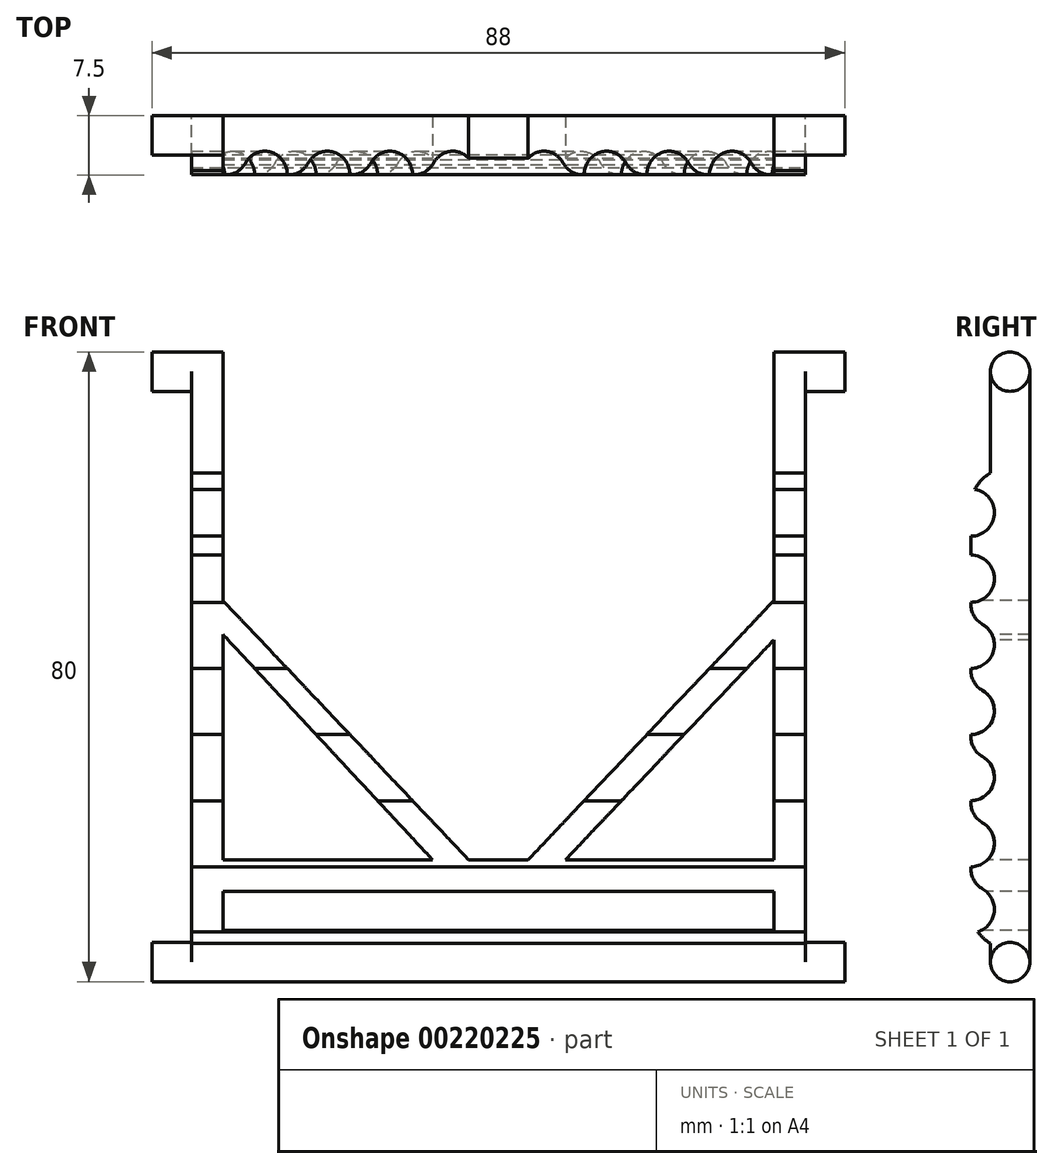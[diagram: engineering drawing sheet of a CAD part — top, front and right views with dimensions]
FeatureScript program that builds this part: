
annotation { "Feature Type Name" : "Feature", "Feature Type Description" : "" }
export const myFeature = defineFeature(function(context is Context, id is Id, definition is map)
    precondition{}
    {
        {
            var Q0;
            Q0=qCreatedBy(makeId("Right.planeOp"),FACE);
            var sketch = newSketch(context, id + "F0", { "sketchPlane" : qUnion([Q0])});
            skLineSegment(sketch, "E0.bottom", {"start": v(-4.18, 3.38) * mm, "end": v(0.82, 3.38) * mm});
            skLineSegment(sketch, "E0.top", {"start": v(-4.18, -71.62) * mm, "end": v(0.82, -71.62) * mm});
            skLineSegment(sketch, "E0.left", {"start": v(-4.18, 3.38) * mm, "end": v(-4.18, -71.62) * mm});
            skLineSegment(sketch, "E0.right", {"start": v(0.82, 3.38) * mm, "end": v(0.82, -71.62) * mm});
            skCircle(sketch, "E1", {"center": v(-1.68, 3.38) * mm, "radius": 2.5 * mm});
            skCircle(sketch, "E2", {"center": v(-1.68, -71.62) * mm, "radius": 2.5 * mm});
            skLineSegment(sketch, "E3.bottom", {"start": v(-4.18, -69.26) * mm, "end": v(-6.68, -69.26) * mm});
            skLineSegment(sketch, "E3.top", {"start": v(-4.18, -9.5) * mm, "end": v(-6.68, -9.5) * mm});
            skLineSegment(sketch, "E3.left", {"start": v(-4.18, -69.26) * mm, "end": v(-4.18, -9.5) * mm});
            skLineSegment(sketch, "E3.right", {"start": v(-6.68, -69.26) * mm, "end": v(-6.68, -9.5) * mm});
            skSolve(sketch);
        }
        {
            var Q0;
            {var subQ0=sQuery(id+"F0.wireOp",EDGE,"E0.left");Q0=makeQuery(id+"F0.imprint","IMPRINT",FACE,{"disambiguationData":[TD([[makeQuery(id+"F0.imprint","IMPRINT",EDGE,{"derivedFrom":subQ0}),1.0]])]});}
            extrude(context, id + "F1", {"entities" : qUnion([Q0]), "endBound" : BoundingType.SYMMETRIC, "depth" : 78 * mm});
        }
        {
            var Q0;
            Q0=makeQuery(id+"F0.imprint","IMPRINT",FACE,{"disambiguationData":[TD([[makeQuery(id+"F0.imprint","IMPRINT",EDGE,{"derivedFrom":sQuery(id+"F0.wireOp",EDGE,"E3.bottom")}),-1.0]])]});
            extrude(context, id + "F2", {"entities" : qUnion([Q0]), "operationType" : NewBodyOperationType.ADD, "endBound" : BoundingType.SYMMETRIC, "depth" : 78 * mm});
        }
        {
            var Q0;
            {var subQ0=sQuery(id+"F0.wireOp",EDGE,"E0.bottom");Q0=makeQuery(id+"F0.imprint","IMPRINT",FACE,{"disambiguationData":[TD([[makeQuery(id+"F0.imprint","IMPRINT",EDGE,{"derivedFrom":subQ0}),1.0]])]});}
            var Q1;
            {var subQ0=sQuery(id+"F0.wireOp",EDGE,"E0.bottom");Q1=makeQuery(id+"F0.imprint","IMPRINT",FACE,{"disambiguationData":[TD([[makeQuery(id+"F0.imprint","IMPRINT",EDGE,{"derivedFrom":subQ0}),-1.0]])]});}
            var Q2;
            {var subQ0=sQuery(id+"F0.wireOp",EDGE,"E0.top");Q2=makeQuery(id+"F0.imprint","IMPRINT",FACE,{"disambiguationData":[TD([[makeQuery(id+"F0.imprint","IMPRINT",EDGE,{"derivedFrom":subQ0}),-1.0]])]});}
            var Q3;
            {var subQ0=sQuery(id+"F0.wireOp",EDGE,"E0.top");Q3=makeQuery(id+"F0.imprint","IMPRINT",FACE,{"disambiguationData":[TD([[makeQuery(id+"F0.imprint","IMPRINT",EDGE,{"derivedFrom":subQ0}),1.0]])]});}
            extrude(context, id + "F3", {"entities" : qUnion([Q0, Q1, Q2, Q3]), "operationType" : NewBodyOperationType.ADD, "endBound" : BoundingType.SYMMETRIC, "depth" : 88 * mm});
        }
        {
            var Q0;
            Q0=makeQuery(id+"F1.opExtrude","SWEPT_FACE",FACE,{"disambiguationData":[OSD([sQuery(id+"F0.wireOp",EDGE,"E0.right")])]});
            var sketch = newSketch(context, id + "F4", { "sketchPlane" : qUnion([Q0])});
            skLineSegment(sketch, "E4.0", {"start": v(39, 3.38) * mm, "end": v(39, -71.62) * mm});
            skLineSegment(sketch, "E4.1", {"start": v(39, 3.38) * mm, "end": v(39, -9.5) * mm});
            skLineSegment(sketch, "E5.bottom", {"start": v(-35, -62.62) * mm, "end": v(35, -62.62) * mm});
            skLineSegment(sketch, "E5.top", {"start": v(-35, -67.62) * mm, "end": v(35, -67.62) * mm});
            skLineSegment(sketch, "E5.left", {"start": v(-35, -62.62) * mm, "end": v(-35, -67.62) * mm});
            skLineSegment(sketch, "E5.right", {"start": v(35, -62.62) * mm, "end": v(35, -67.62) * mm});
            skLineSegment(sketch, "E6.bottom", {"start": v(35, 7.25) * mm, "end": v(-35, 7.25) * mm});
            skLineSegment(sketch, "E6.top", {"start": v(35, -58.62) * mm, "end": v(-35, -58.62) * mm});
            skLineSegment(sketch, "E6.left", {"start": v(35, 7.25) * mm, "end": v(35, -58.62) * mm});
            skLineSegment(sketch, "E6.right", {"start": v(-35, 7.25) * mm, "end": v(-35, -58.62) * mm});
            skLineSegment(sketch, "E7", {"start": v(-35, -25.69) * mm, "end": v(0, -62.62) * mm});
            skLineSegment(sketch, "E8", {"start": v(0, -62.62) * mm, "end": v(35, -25.69) * mm});
            skLineSegment(sketch, "E9", {"start": v(35, -25.69) * mm, "end": v(39, -25.69) * mm});
            skLineSegment(sketch, "E10", {"start": v(39, -25.69) * mm, "end": v(0, -67.62) * mm});
            skLineSegment(sketch, "E11", {"start": v(0, -67.62) * mm, "end": v(-39.74, -25.69) * mm});
            skLineSegment(sketch, "E12", {"start": v(-39.74, -25.69) * mm, "end": v(-35, -25.69) * mm});
            skSolve(sketch);
        }
        {
            var Q0;
            {var subQ0=sQuery(id+"F0.wireOp",EDGE,"E3.top");var subQ1=sQuery(id+"F0.wireOp",EDGE,"E3.right");Q0=makeQuery(id+"F17sXBwQNLpgOEj_1.boolean.opBoolean","SPLIT",EDGE,{"disambiguationData":[TD([makeQuery(id+"F17sXBwQNLpgOEj_1.opExtrude","SWEPT_FACE",FACE,{"disambiguationData":[OSD([sQuery(id+"F4.wireOp",EDGE,"E6.left")])]})])],"derivedFrom":makeQuery(id+"F2.opExtrude","SWEPT_EDGE",EDGE,{"disambiguationData":[OSD([subQ0,subQ1])]})});}
            var Q1;
            {var subQ0=sQuery(id+"F0.wireOp",EDGE,"E3.top");var subQ1=sQuery(id+"F0.wireOp",EDGE,"E3.right");Q1=makeQuery(id+"F17sXBwQNLpgOEj_1.boolean.opBoolean","SPLIT",EDGE,{"disambiguationData":[TD([makeQuery(id+"F17sXBwQNLpgOEj_1.opExtrude","SWEPT_FACE",FACE,{"disambiguationData":[OSD([sQuery(id+"F4.wireOp",EDGE,"E6.right")])]})])],"derivedFrom":makeQuery(id+"F2.opExtrude","SWEPT_EDGE",EDGE,{"disambiguationData":[OSD([subQ0,subQ1])]})});}
            var Q2;
            Q2=makeQuery(id+"F2.opExtrude","SWEPT_EDGE",EDGE,{"disambiguationData":[OSD([sQuery(id+"F0.wireOp",EDGE,"E3.bottom"),sQuery(id+"F0.wireOp",EDGE,"E3.right")])]});
            fillet(context, id + "F5", {"entities" : qUnion([Q0, Q1, Q2]), "radius" : 5 * mm, "tangentPropagation" : true, "allowEdgeOverflow" : false});
        }
        {
            var Q0;
            {var subQ0=sQuery(id+"F0.wireOp",EDGE,"E3.left");Q0=makeQuery(id+"F2.boolean.opBoolean","MERGE",FACE,{"derivedFrom":[makeQuery(id+"F1.opExtrude","CAP_FACE",FACE,{"disambiguationData":[OSD([sQuery(id+"F0.wireOp",EDGE,"E0.left"),sQuery(id+"F0.wireOp",EDGE,"E0.right"),sQuery(id+"F0.wireOp",EDGE,"E1"),sQuery(id+"F0.wireOp",EDGE,"E2"),subQ0])],"isStart":false}),makeQuery(id+"F2.opExtrude","CAP_FACE",FACE,{"disambiguationData":[OSD([sQuery(id+"F0.wireOp",EDGE,"E3.bottom"),sQuery(id+"F0.wireOp",EDGE,"E3.top"),subQ0,sQuery(id+"F0.wireOp",EDGE,"E3.right")])],"isStart":false})]});}
            var sketch = newSketch(context, id + "F6", { "sketchPlane" : qUnion([Q0])});
            skCircle(sketch, "E13", {"center": v(-6.68, -64.93) * mm, "radius": 3 * mm});
            skCircle(sketch, "E14.0.1.0", {"center": v(-6.68, -56.53) * mm, "radius": 3 * mm});
            skCircle(sketch, "E14.0.2.0", {"center": v(-6.68, -48.13) * mm, "radius": 3 * mm});
            skCircle(sketch, "E14.0.3.0", {"center": v(-6.68, -39.73) * mm, "radius": 3 * mm});
            skCircle(sketch, "E14.0.4.0", {"center": v(-6.68, -31.33) * mm, "radius": 3 * mm});
            skCircle(sketch, "E14.0.5.0", {"center": v(-6.68, -22.93) * mm, "radius": 3 * mm});
            skCircle(sketch, "E14.0.6.0", {"center": v(-6.68, -14.53) * mm, "radius": 3 * mm});
            skLineSegment(sketch, "E14.direction1", {"start": v(-6.68, -64.93) * mm, "end": v(18.32, -64.93) * mm, "construction": true});
            skLineSegment(sketch, "E14.direction2", {"start": v(-6.68, -64.93) * mm, "end": v(-6.68, -56.53) * mm, "construction": true});
            skSolve(sketch);
        }
        {
            var Q0;
            {var subQ0=sQuery(id+"F6.wireOp",EDGE,"E13");var subQ1=sQuery(id+"F0.wireOp",EDGE,"E3.right");var subQ6=makeQuery(id+"F2.opExtrude","CAP_EDGE",EDGE,{"disambiguationData":[OSD([subQ1])],"isStart":false});var subQ7=makeQuery(id+"F6.imprint","INTERSECT",VERTEX,{"derivedFrom":[subQ6,subQ0]});Q0=makeQuery(id+"F6.imprint","IMPRINT",FACE,{"disambiguationData":[TD([[makeQuery(id+"F6.imprint","IMPRINT",EDGE,{"disambiguationData":[TD([[subQ7,1.0]])],"derivedFrom":subQ0}),1.0]])]});}
            var Q1;
            {var subQ0=sQuery(id+"F6.wireOp",EDGE,"E14.0.1.0");var subQ1=makeQuery(id+"F2.opExtrude","CAP_EDGE",EDGE,{"disambiguationData":[OSD([sQuery(id+"F0.wireOp",EDGE,"E3.right")])],"isStart":false});var subQ2=makeQuery(id+"F6.imprint","INTERSECT",VERTEX,{"disambiguationData":[OD(0.0)],"derivedFrom":[subQ1,subQ0]});Q1=makeQuery(id+"F6.imprint","IMPRINT",FACE,{"disambiguationData":[TD([[makeQuery(id+"F6.imprint","IMPRINT",EDGE,{"disambiguationData":[TD([[subQ2,-1.0]])],"derivedFrom":subQ0}),1.0]])]});}
            var Q2;
            {var subQ0=sQuery(id+"F6.wireOp",EDGE,"E14.0.2.0");var subQ1=makeQuery(id+"F2.opExtrude","CAP_EDGE",EDGE,{"disambiguationData":[OSD([sQuery(id+"F0.wireOp",EDGE,"E3.right")])],"isStart":false});var subQ2=makeQuery(id+"F6.imprint","INTERSECT",VERTEX,{"disambiguationData":[OD(0.0)],"derivedFrom":[subQ1,subQ0]});Q2=makeQuery(id+"F6.imprint","IMPRINT",FACE,{"disambiguationData":[TD([[makeQuery(id+"F6.imprint","IMPRINT",EDGE,{"disambiguationData":[TD([[subQ2,-1.0]])],"derivedFrom":subQ0}),1.0]])]});}
            var Q3;
            {var subQ0=sQuery(id+"F6.wireOp",EDGE,"E14.0.3.0");var subQ1=makeQuery(id+"F2.opExtrude","CAP_EDGE",EDGE,{"disambiguationData":[OSD([sQuery(id+"F0.wireOp",EDGE,"E3.right")])],"isStart":false});var subQ2=makeQuery(id+"F6.imprint","INTERSECT",VERTEX,{"disambiguationData":[OD(0.0)],"derivedFrom":[subQ1,subQ0]});Q3=makeQuery(id+"F6.imprint","IMPRINT",FACE,{"disambiguationData":[TD([[makeQuery(id+"F6.imprint","IMPRINT",EDGE,{"disambiguationData":[TD([[subQ2,-1.0]])],"derivedFrom":subQ0}),1.0]])]});}
            var Q4;
            {var subQ0=sQuery(id+"F6.wireOp",EDGE,"E14.0.4.0");var subQ1=makeQuery(id+"F2.opExtrude","CAP_EDGE",EDGE,{"disambiguationData":[OSD([sQuery(id+"F0.wireOp",EDGE,"E3.right")])],"isStart":false});var subQ2=makeQuery(id+"F6.imprint","INTERSECT",VERTEX,{"disambiguationData":[OD(0.0)],"derivedFrom":[subQ1,subQ0]});Q4=makeQuery(id+"F6.imprint","IMPRINT",FACE,{"disambiguationData":[TD([[makeQuery(id+"F6.imprint","IMPRINT",EDGE,{"disambiguationData":[TD([[subQ2,1.0]])],"derivedFrom":subQ0}),1.0]])]});}
            var Q5;
            {var subQ0=sQuery(id+"F6.wireOp",EDGE,"E14.0.5.0");var subQ1=makeQuery(id+"F2.opExtrude","CAP_EDGE",EDGE,{"disambiguationData":[OSD([sQuery(id+"F0.wireOp",EDGE,"E3.right")])],"isStart":false});var subQ2=makeQuery(id+"F6.imprint","INTERSECT",VERTEX,{"disambiguationData":[OD(0.0)],"derivedFrom":[subQ1,subQ0]});Q5=makeQuery(id+"F6.imprint","IMPRINT",FACE,{"disambiguationData":[TD([[makeQuery(id+"F6.imprint","IMPRINT",EDGE,{"disambiguationData":[TD([[subQ2,1.0]])],"derivedFrom":subQ0}),1.0]])]});}
            var Q6;
            {var subQ0=sQuery(id+"F6.wireOp",EDGE,"E14.0.6.0");var subQ1=sQuery(id+"F0.wireOp",EDGE,"E3.right");var subQ8=makeQuery(id+"F2.opExtrude","CAP_EDGE",EDGE,{"disambiguationData":[OSD([subQ1])],"isStart":false});var subQ9=makeQuery(id+"F6.imprint","INTERSECT",VERTEX,{"derivedFrom":[subQ8,subQ0]});Q6=makeQuery(id+"F6.imprint","IMPRINT",FACE,{"disambiguationData":[TD([[makeQuery(id+"F6.imprint","IMPRINT",EDGE,{"disambiguationData":[TD([[subQ9,-1.0]])],"derivedFrom":subQ0}),1.0]])]});}
            extrude(context, id + "F7", {"entities" : qUnion([Q0, Q1, Q2, Q3, Q4, Q5, Q6]), "operationType" : NewBodyOperationType.REMOVE, "endBound" : BoundingType.THROUGH_ALL, "oppositeDirection" : true, "depth" : 25 * mm});
        }
        {
            var Q0;
            {var subQ3=sQuery(id+"F4.wireOp",EDGE,"E6.top");var subQ5=sQuery(id+"F4.wireOp",EDGE,"E8");var subQ6=makeQuery(id+"F4.imprint","INTERSECT",VERTEX,{"derivedFrom":[subQ3,subQ5]});Q0=makeQuery(id+"F4.imprint","IMPRINT",FACE,{"disambiguationData":[TD([[makeQuery(id+"F4.imprint","IMPRINT",EDGE,{"disambiguationData":[TD([[subQ6,-1.0]])],"derivedFrom":subQ3}),-1.0]])]});}
            var Q1;
            {var subQ0=sQuery(id+"F4.wireOp",EDGE,"E6.bottom");Q1=makeQuery(id+"F4.imprint","IMPRINT",FACE,{"disambiguationData":[TD([[makeQuery(id+"F4.imprint","IMPRINT",EDGE,{"derivedFrom":subQ0}),1.0]])]});}
            var Q2;
            {var subQ0=sQuery(id+"F4.wireOp",EDGE,"E6.right");var subQ1=sQuery(id+"F4.wireOp",EDGE,"E6.top");var subQ2=makeQuery(id+"F4.imprint","INTERSECT",VERTEX,{"derivedFrom":[subQ1,subQ0]});Q2=makeQuery(id+"F4.imprint","IMPRINT",FACE,{"disambiguationData":[TD([[makeQuery(id+"F4.imprint","IMPRINT",EDGE,{"disambiguationData":[TD([[subQ2,1.0]])],"derivedFrom":subQ1}),-1.0]])]});}
            var Q3;
            {var subQ0=sQuery(id+"F4.wireOp",EDGE,"E5.left");Q3=makeQuery(id+"F4.imprint","IMPRINT",FACE,{"disambiguationData":[TD([[makeQuery(id+"F4.imprint","IMPRINT",EDGE,{"derivedFrom":subQ0}),1.0]])]});}
            var Q4;
            {var subQ0=sQuery(id+"F4.wireOp",EDGE,"E5.right");Q4=makeQuery(id+"F4.imprint","IMPRINT",FACE,{"disambiguationData":[TD([[makeQuery(id+"F4.imprint","IMPRINT",EDGE,{"derivedFrom":subQ0}),-1.0]])]});}
            var Q5;
            {var subQ0=sQuery(id+"F4.wireOp",EDGE,"E6.left");var subQ1=sQuery(id+"F4.wireOp",EDGE,"E6.top");var subQ2=makeQuery(id+"F4.imprint","INTERSECT",VERTEX,{"derivedFrom":[subQ1,subQ0]});Q5=makeQuery(id+"F4.imprint","IMPRINT",FACE,{"disambiguationData":[TD([[makeQuery(id+"F4.imprint","IMPRINT",EDGE,{"disambiguationData":[TD([[subQ2,-1.0]])],"derivedFrom":subQ1}),-1.0]])]});}
            var Q6;
            {var subQ0=sQuery(id+"F4.wireOp",EDGE,"E5.bottom");var subQ2=sQuery(id+"F4.wireOp",EDGE,"E11");var subQ3=makeQuery(id+"F4.imprint","INTERSECT",VERTEX,{"derivedFrom":[subQ0,subQ2]});Q6=makeQuery(id+"F4.imprint","IMPRINT",FACE,{"disambiguationData":[TD([[makeQuery(id+"F4.imprint","IMPRINT",EDGE,{"disambiguationData":[TD([[subQ3,-1.0]])],"derivedFrom":subQ0}),-1.0]])]});}
            extrude(context, id + "F8", {"entities" : qUnion([Q0, Q1, Q2, Q3, Q4, Q5, Q6]), "operationType" : NewBodyOperationType.REMOVE, "endBound" : BoundingType.SYMMETRIC, "depth" : 25 * mm});
        }
        {
            var Q0;
            {var subQ0=sQuery(id+"F6.wireOp",EDGE,"E14.0.6.0");var subQ1=sQuery(id+"F0.wireOp",EDGE,"E3.right");var subQ2=sQuery(id+"F0.wireOp",EDGE,"E3.top");var subQ3=sQuery(id+"F0.wireOp",EDGE,"E3.left");var subQ4=sQuery(id+"F0.wireOp",EDGE,"E3.bottom");var subQ5=sQuery(id+"F0.wireOp",EDGE,"E2");var subQ6=sQuery(id+"F0.wireOp",EDGE,"E1");var subQ7=sQuery(id+"F0.wireOp",EDGE,"E0.right");var subQ8=sQuery(id+"F0.wireOp",EDGE,"E0.left");Q0=makeQuery(id+"F8.boolean.opBoolean","SPLIT",EDGE,{"disambiguationData":[TD([makeQuery(id+"F2.opExtrude","CAP_FACE",FACE,{"disambiguationData":[OSD([subQ4,subQ2,subQ3,subQ1])],"isStart":true})])],"derivedFrom":makeQuery(id+"F7.boolean.opBoolean","COPY",EDGE,{"derivedFrom":makeQuery(id+"F7.opExtrude","SWEPT_EDGE",EDGE,{"disambiguationData":[OSD([subQ8,subQ7,subQ6,subQ5,subQ4,subQ2,subQ3,subQ1,subQ0])]})})});}
            var Q1;
            {var subQ0=sQuery(id+"F6.wireOp",EDGE,"E14.0.5.0");var subQ1=sQuery(id+"F0.wireOp",EDGE,"E3.right");var subQ2=sQuery(id+"F0.wireOp",EDGE,"E3.left");Q1=makeQuery(id+"F8.boolean.opBoolean","SPLIT",EDGE,{"disambiguationData":[TD([makeQuery(id+"F2.opExtrude","CAP_FACE",FACE,{"disambiguationData":[OSD([sQuery(id+"F0.wireOp",EDGE,"E3.bottom"),sQuery(id+"F0.wireOp",EDGE,"E3.top"),subQ2,subQ1])],"isStart":true})])],"derivedFrom":makeQuery(id+"F7.boolean.opBoolean","COPY",EDGE,{"derivedFrom":makeQuery(id+"F7.opExtrude","SWEPT_EDGE",EDGE,{"disambiguationData":[OSD([subQ1,subQ0]),TDD([makeQuery(id+"F6.imprint","INTERSECT",VERTEX,{"disambiguationData":[OD(0.0)],"derivedFrom":[makeQuery(id+"F2.opExtrude","CAP_EDGE",EDGE,{"disambiguationData":[OSD([subQ1])],"isStart":false}),subQ0]})])]})})});}
            var Q2;
            {var subQ0=sQuery(id+"F6.wireOp",EDGE,"E14.0.4.0");var subQ1=sQuery(id+"F0.wireOp",EDGE,"E3.right");Q2=makeQuery(id+"F8.boolean.opBoolean","SPLIT",EDGE,{"disambiguationData":[TD([makeQuery(id+"F8.opExtrude","SWEPT_FACE",FACE,{"disambiguationData":[OSD([sQuery(id+"F4.wireOp",EDGE,"E8")])]})])],"derivedFrom":makeQuery(id+"F7.boolean.opBoolean","COPY",EDGE,{"derivedFrom":makeQuery(id+"F7.opExtrude","SWEPT_EDGE",EDGE,{"disambiguationData":[OSD([subQ1,subQ0]),TDD([makeQuery(id+"F6.imprint","INTERSECT",VERTEX,{"disambiguationData":[OD(0.0)],"derivedFrom":[makeQuery(id+"F2.opExtrude","CAP_EDGE",EDGE,{"disambiguationData":[OSD([subQ1])],"isStart":false}),subQ0]})])]})})});}
            var Q3;
            {var subQ0=sQuery(id+"F0.wireOp",EDGE,"E3.right");var subQ2=sQuery(id+"F6.wireOp",EDGE,"E14.0.3.0");var subQ3=sQuery(id+"F4.wireOp",EDGE,"E6.left");Q3=makeQuery(id+"F8.boolean.opBoolean","SPLIT",EDGE,{"disambiguationData":[TD([makeQuery(id+"F8.opExtrude","SWEPT_FACE",FACE,{"disambiguationData":[OSD([subQ3]),TDD([makeQuery(id+"F4.imprint","IMPRINT",EDGE,{"disambiguationData":[TD([[makeQuery(id+"F4.imprint","INTERSECT",VERTEX,{"derivedFrom":[sQuery(id+"F4.wireOp",EDGE,"E6.top"),subQ3]}),1.0]])],"derivedFrom":subQ3})])]})])],"derivedFrom":makeQuery(id+"F7.boolean.opBoolean","COPY",EDGE,{"derivedFrom":makeQuery(id+"F7.opExtrude","SWEPT_EDGE",EDGE,{"disambiguationData":[OSD([subQ0,subQ2]),TDD([makeQuery(id+"F6.imprint","INTERSECT",VERTEX,{"disambiguationData":[OD(1.0)],"derivedFrom":[makeQuery(id+"F2.opExtrude","CAP_EDGE",EDGE,{"disambiguationData":[OSD([subQ0])],"isStart":false}),subQ2]})])]})})});}
            var Q4;
            {var subQ0=sQuery(id+"F6.wireOp",EDGE,"E14.0.2.0");var subQ1=sQuery(id+"F0.wireOp",EDGE,"E3.right");var subQ3=sQuery(id+"F4.wireOp",EDGE,"E6.left");Q4=makeQuery(id+"F8.boolean.opBoolean","SPLIT",EDGE,{"disambiguationData":[TD([makeQuery(id+"F8.opExtrude","SWEPT_FACE",FACE,{"disambiguationData":[OSD([subQ3]),TDD([makeQuery(id+"F4.imprint","IMPRINT",EDGE,{"disambiguationData":[TD([[makeQuery(id+"F4.imprint","INTERSECT",VERTEX,{"derivedFrom":[sQuery(id+"F4.wireOp",EDGE,"E6.top"),subQ3]}),1.0]])],"derivedFrom":subQ3})])]})])],"derivedFrom":makeQuery(id+"F7.boolean.opBoolean","COPY",EDGE,{"derivedFrom":makeQuery(id+"F7.opExtrude","SWEPT_EDGE",EDGE,{"disambiguationData":[OSD([subQ1,subQ0]),TDD([makeQuery(id+"F6.imprint","INTERSECT",VERTEX,{"disambiguationData":[OD(1.0)],"derivedFrom":[makeQuery(id+"F2.opExtrude","CAP_EDGE",EDGE,{"disambiguationData":[OSD([subQ1])],"isStart":false}),subQ0]})])]})})});}
            var Q5;
            {var subQ0=sQuery(id+"F6.wireOp",EDGE,"E14.0.1.0");var subQ1=sQuery(id+"F0.wireOp",EDGE,"E3.right");var subQ3=sQuery(id+"F4.wireOp",EDGE,"E6.left");Q5=makeQuery(id+"F8.boolean.opBoolean","SPLIT",EDGE,{"disambiguationData":[TD([makeQuery(id+"F8.opExtrude","SWEPT_FACE",FACE,{"disambiguationData":[OSD([subQ3]),TDD([makeQuery(id+"F4.imprint","IMPRINT",EDGE,{"disambiguationData":[TD([[makeQuery(id+"F4.imprint","INTERSECT",VERTEX,{"derivedFrom":[sQuery(id+"F4.wireOp",EDGE,"E6.top"),subQ3]}),1.0]])],"derivedFrom":subQ3})])]})])],"derivedFrom":makeQuery(id+"F7.boolean.opBoolean","COPY",EDGE,{"derivedFrom":makeQuery(id+"F7.opExtrude","SWEPT_EDGE",EDGE,{"disambiguationData":[OSD([subQ1,subQ0]),TDD([makeQuery(id+"F6.imprint","INTERSECT",VERTEX,{"disambiguationData":[OD(1.0)],"derivedFrom":[makeQuery(id+"F2.opExtrude","CAP_EDGE",EDGE,{"disambiguationData":[OSD([subQ1])],"isStart":false}),subQ0]})])]})})});}
            var Q6;
            {var subQ0=sQuery(id+"F0.wireOp",EDGE,"E3.right");var subQ1=sQuery(id+"F6.wireOp",EDGE,"E14.0.1.0");Q6=makeQuery(id+"F8.boolean.opBoolean","SPLIT",EDGE,{"disambiguationData":[TD([makeQuery(id+"F8.opExtrude","SWEPT_FACE",FACE,{"disambiguationData":[OSD([sQuery(id+"F4.wireOp",EDGE,"E8")])]})])],"derivedFrom":makeQuery(id+"F7.boolean.opBoolean","COPY",EDGE,{"derivedFrom":makeQuery(id+"F7.opExtrude","SWEPT_EDGE",EDGE,{"disambiguationData":[OSD([subQ0,subQ1]),TDD([makeQuery(id+"F6.imprint","INTERSECT",VERTEX,{"disambiguationData":[OD(1.0)],"derivedFrom":[makeQuery(id+"F2.opExtrude","CAP_EDGE",EDGE,{"disambiguationData":[OSD([subQ0])],"isStart":false}),subQ1]})])]})})});}
            var Q7;
            {var subQ0=sQuery(id+"F0.wireOp",EDGE,"E3.right");var subQ1=sQuery(id+"F6.wireOp",EDGE,"E14.0.2.0");Q7=makeQuery(id+"F8.boolean.opBoolean","SPLIT",EDGE,{"disambiguationData":[TD([makeQuery(id+"F8.opExtrude","SWEPT_FACE",FACE,{"disambiguationData":[OSD([sQuery(id+"F4.wireOp",EDGE,"E8")])]})])],"derivedFrom":makeQuery(id+"F7.boolean.opBoolean","COPY",EDGE,{"derivedFrom":makeQuery(id+"F7.opExtrude","SWEPT_EDGE",EDGE,{"disambiguationData":[OSD([subQ0,subQ1]),TDD([makeQuery(id+"F6.imprint","INTERSECT",VERTEX,{"disambiguationData":[OD(1.0)],"derivedFrom":[makeQuery(id+"F2.opExtrude","CAP_EDGE",EDGE,{"disambiguationData":[OSD([subQ0])],"isStart":false}),subQ1]})])]})})});}
            var Q8;
            {var subQ0=sQuery(id+"F0.wireOp",EDGE,"E3.right");var subQ1=sQuery(id+"F6.wireOp",EDGE,"E14.0.3.0");Q8=makeQuery(id+"F8.boolean.opBoolean","SPLIT",EDGE,{"disambiguationData":[TD([makeQuery(id+"F8.opExtrude","SWEPT_FACE",FACE,{"disambiguationData":[OSD([sQuery(id+"F4.wireOp",EDGE,"E8")])]})])],"derivedFrom":makeQuery(id+"F7.boolean.opBoolean","COPY",EDGE,{"derivedFrom":makeQuery(id+"F7.opExtrude","SWEPT_EDGE",EDGE,{"disambiguationData":[OSD([subQ0,subQ1]),TDD([makeQuery(id+"F6.imprint","INTERSECT",VERTEX,{"disambiguationData":[OD(1.0)],"derivedFrom":[makeQuery(id+"F2.opExtrude","CAP_EDGE",EDGE,{"disambiguationData":[OSD([subQ0])],"isStart":false}),subQ1]})])]})})});}
            var Q9;
            {var subQ0=sQuery(id+"F6.wireOp",EDGE,"E14.0.6.0");var subQ1=sQuery(id+"F0.wireOp",EDGE,"E3.right");var subQ2=sQuery(id+"F0.wireOp",EDGE,"E3.top");var subQ4=sQuery(id+"F0.wireOp",EDGE,"E1");var subQ5=sQuery(id+"F0.wireOp",EDGE,"E0.right");var subQ7=sQuery(id+"F0.wireOp",EDGE,"E3.left");var subQ8=sQuery(id+"F0.wireOp",EDGE,"E3.bottom");var subQ9=sQuery(id+"F0.wireOp",EDGE,"E2");var subQ10=sQuery(id+"F0.wireOp",EDGE,"E0.left");Q9=makeQuery(id+"F8.boolean.opBoolean","SPLIT",EDGE,{"disambiguationData":[TD([makeQuery(id+"F2.opExtrude","CAP_FACE",FACE,{"disambiguationData":[OSD([subQ8,subQ2,subQ7,subQ1])],"isStart":false})])],"derivedFrom":makeQuery(id+"F7.boolean.opBoolean","COPY",EDGE,{"derivedFrom":makeQuery(id+"F7.opExtrude","SWEPT_EDGE",EDGE,{"disambiguationData":[OSD([subQ10,subQ5,subQ4,subQ9,subQ8,subQ2,subQ7,subQ1,subQ0])]})})});}
            var Q10;
            {var subQ0=sQuery(id+"F6.wireOp",EDGE,"E14.0.5.0");var subQ1=sQuery(id+"F0.wireOp",EDGE,"E3.left");var subQ4=sQuery(id+"F0.wireOp",EDGE,"E3.right");Q10=makeQuery(id+"F8.boolean.opBoolean","SPLIT",EDGE,{"disambiguationData":[TD([makeQuery(id+"F2.opExtrude","CAP_FACE",FACE,{"disambiguationData":[OSD([sQuery(id+"F0.wireOp",EDGE,"E3.bottom"),sQuery(id+"F0.wireOp",EDGE,"E3.top"),subQ1,subQ4])],"isStart":false})])],"derivedFrom":makeQuery(id+"F7.boolean.opBoolean","COPY",EDGE,{"derivedFrom":makeQuery(id+"F7.opExtrude","SWEPT_EDGE",EDGE,{"disambiguationData":[OSD([subQ4,subQ0]),TDD([makeQuery(id+"F6.imprint","INTERSECT",VERTEX,{"disambiguationData":[OD(0.0)],"derivedFrom":[makeQuery(id+"F2.opExtrude","CAP_EDGE",EDGE,{"disambiguationData":[OSD([subQ4])],"isStart":false}),subQ0]})])]})})});}
            var Q11;
            {var subQ0=sQuery(id+"F6.wireOp",EDGE,"E14.0.4.0");var subQ1=sQuery(id+"F0.wireOp",EDGE,"E3.right");Q11=makeQuery(id+"F8.boolean.opBoolean","SPLIT",EDGE,{"disambiguationData":[TD([makeQuery(id+"F8.opExtrude","SWEPT_FACE",FACE,{"disambiguationData":[OSD([sQuery(id+"F4.wireOp",EDGE,"E7")])]})])],"derivedFrom":makeQuery(id+"F7.boolean.opBoolean","COPY",EDGE,{"derivedFrom":makeQuery(id+"F7.opExtrude","SWEPT_EDGE",EDGE,{"disambiguationData":[OSD([subQ1,subQ0]),TDD([makeQuery(id+"F6.imprint","INTERSECT",VERTEX,{"disambiguationData":[OD(0.0)],"derivedFrom":[makeQuery(id+"F2.opExtrude","CAP_EDGE",EDGE,{"disambiguationData":[OSD([subQ1])],"isStart":false}),subQ0]})])]})})});}
            var Q12;
            {var subQ0=sQuery(id+"F0.wireOp",EDGE,"E3.right");var subQ1=sQuery(id+"F6.wireOp",EDGE,"E14.0.3.0");Q12=makeQuery(id+"F8.boolean.opBoolean","SPLIT",EDGE,{"disambiguationData":[TD([makeQuery(id+"F8.opExtrude","SWEPT_FACE",FACE,{"disambiguationData":[OSD([sQuery(id+"F4.wireOp",EDGE,"E7")])]})])],"derivedFrom":makeQuery(id+"F7.boolean.opBoolean","COPY",EDGE,{"derivedFrom":makeQuery(id+"F7.opExtrude","SWEPT_EDGE",EDGE,{"disambiguationData":[OSD([subQ0,subQ1]),TDD([makeQuery(id+"F6.imprint","INTERSECT",VERTEX,{"disambiguationData":[OD(1.0)],"derivedFrom":[makeQuery(id+"F2.opExtrude","CAP_EDGE",EDGE,{"disambiguationData":[OSD([subQ0])],"isStart":false}),subQ1]})])]})})});}
            var Q13;
            {var subQ0=sQuery(id+"F0.wireOp",EDGE,"E3.right");var subQ2=sQuery(id+"F6.wireOp",EDGE,"E14.0.3.0");var subQ3=sQuery(id+"F4.wireOp",EDGE,"E6.right");Q13=makeQuery(id+"F8.boolean.opBoolean","SPLIT",EDGE,{"disambiguationData":[TD([makeQuery(id+"F8.opExtrude","SWEPT_FACE",FACE,{"disambiguationData":[OSD([subQ3]),TDD([makeQuery(id+"F4.imprint","IMPRINT",EDGE,{"disambiguationData":[TD([[makeQuery(id+"F4.imprint","INTERSECT",VERTEX,{"derivedFrom":[sQuery(id+"F4.wireOp",EDGE,"E6.top"),subQ3]}),1.0]])],"derivedFrom":subQ3})])]})])],"derivedFrom":makeQuery(id+"F7.boolean.opBoolean","COPY",EDGE,{"derivedFrom":makeQuery(id+"F7.opExtrude","SWEPT_EDGE",EDGE,{"disambiguationData":[OSD([subQ0,subQ2]),TDD([makeQuery(id+"F6.imprint","INTERSECT",VERTEX,{"disambiguationData":[OD(1.0)],"derivedFrom":[makeQuery(id+"F2.opExtrude","CAP_EDGE",EDGE,{"disambiguationData":[OSD([subQ0])],"isStart":false}),subQ2]})])]})})});}
            var Q14;
            {var subQ0=sQuery(id+"F6.wireOp",EDGE,"E14.0.2.0");var subQ1=sQuery(id+"F0.wireOp",EDGE,"E3.right");var subQ3=sQuery(id+"F4.wireOp",EDGE,"E6.right");Q14=makeQuery(id+"F8.boolean.opBoolean","SPLIT",EDGE,{"disambiguationData":[TD([makeQuery(id+"F8.opExtrude","SWEPT_FACE",FACE,{"disambiguationData":[OSD([subQ3]),TDD([makeQuery(id+"F4.imprint","IMPRINT",EDGE,{"disambiguationData":[TD([[makeQuery(id+"F4.imprint","INTERSECT",VERTEX,{"derivedFrom":[sQuery(id+"F4.wireOp",EDGE,"E6.top"),subQ3]}),1.0]])],"derivedFrom":subQ3})])]})])],"derivedFrom":makeQuery(id+"F7.boolean.opBoolean","COPY",EDGE,{"derivedFrom":makeQuery(id+"F7.opExtrude","SWEPT_EDGE",EDGE,{"disambiguationData":[OSD([subQ1,subQ0]),TDD([makeQuery(id+"F6.imprint","INTERSECT",VERTEX,{"disambiguationData":[OD(1.0)],"derivedFrom":[makeQuery(id+"F2.opExtrude","CAP_EDGE",EDGE,{"disambiguationData":[OSD([subQ1])],"isStart":false}),subQ0]})])]})})});}
            var Q15;
            {var subQ0=sQuery(id+"F0.wireOp",EDGE,"E3.right");var subQ1=sQuery(id+"F6.wireOp",EDGE,"E14.0.2.0");Q15=makeQuery(id+"F8.boolean.opBoolean","SPLIT",EDGE,{"disambiguationData":[TD([makeQuery(id+"F8.opExtrude","SWEPT_FACE",FACE,{"disambiguationData":[OSD([sQuery(id+"F4.wireOp",EDGE,"E7")])]})])],"derivedFrom":makeQuery(id+"F7.boolean.opBoolean","COPY",EDGE,{"derivedFrom":makeQuery(id+"F7.opExtrude","SWEPT_EDGE",EDGE,{"disambiguationData":[OSD([subQ0,subQ1]),TDD([makeQuery(id+"F6.imprint","INTERSECT",VERTEX,{"disambiguationData":[OD(1.0)],"derivedFrom":[makeQuery(id+"F2.opExtrude","CAP_EDGE",EDGE,{"disambiguationData":[OSD([subQ0])],"isStart":false}),subQ1]})])]})})});}
            var Q16;
            {var subQ0=sQuery(id+"F0.wireOp",EDGE,"E3.right");var subQ1=sQuery(id+"F6.wireOp",EDGE,"E14.0.1.0");Q16=makeQuery(id+"F8.boolean.opBoolean","SPLIT",EDGE,{"disambiguationData":[TD([makeQuery(id+"F8.opExtrude","SWEPT_FACE",FACE,{"disambiguationData":[OSD([sQuery(id+"F4.wireOp",EDGE,"E7")])]})])],"derivedFrom":makeQuery(id+"F7.boolean.opBoolean","COPY",EDGE,{"derivedFrom":makeQuery(id+"F7.opExtrude","SWEPT_EDGE",EDGE,{"disambiguationData":[OSD([subQ0,subQ1]),TDD([makeQuery(id+"F6.imprint","INTERSECT",VERTEX,{"disambiguationData":[OD(1.0)],"derivedFrom":[makeQuery(id+"F2.opExtrude","CAP_EDGE",EDGE,{"disambiguationData":[OSD([subQ0])],"isStart":false}),subQ1]})])]})})});}
            var Q17;
            {var subQ0=sQuery(id+"F6.wireOp",EDGE,"E14.0.1.0");var subQ1=sQuery(id+"F0.wireOp",EDGE,"E3.right");var subQ3=sQuery(id+"F4.wireOp",EDGE,"E6.right");Q17=makeQuery(id+"F8.boolean.opBoolean","SPLIT",EDGE,{"disambiguationData":[TD([makeQuery(id+"F8.opExtrude","SWEPT_FACE",FACE,{"disambiguationData":[OSD([subQ3]),TDD([makeQuery(id+"F4.imprint","IMPRINT",EDGE,{"disambiguationData":[TD([[makeQuery(id+"F4.imprint","INTERSECT",VERTEX,{"derivedFrom":[sQuery(id+"F4.wireOp",EDGE,"E6.top"),subQ3]}),1.0]])],"derivedFrom":subQ3})])]})])],"derivedFrom":makeQuery(id+"F7.boolean.opBoolean","COPY",EDGE,{"derivedFrom":makeQuery(id+"F7.opExtrude","SWEPT_EDGE",EDGE,{"disambiguationData":[OSD([subQ1,subQ0]),TDD([makeQuery(id+"F6.imprint","INTERSECT",VERTEX,{"disambiguationData":[OD(1.0)],"derivedFrom":[makeQuery(id+"F2.opExtrude","CAP_EDGE",EDGE,{"disambiguationData":[OSD([subQ1])],"isStart":false}),subQ0]})])]})})});}
            var Q18;
            Q18=makeQuery(id+"F7.boolean.opBoolean","COPY",EDGE,{"derivedFrom":makeQuery(id+"F7.opExtrude","SWEPT_EDGE",EDGE,{"disambiguationData":[OSD([sQuery(id+"F0.wireOp",EDGE,"E3.right"),sQuery(id+"F6.wireOp",EDGE,"E13")])]})});
            fillet(context, id + "F9", {"entities" : qUnion([Q0, Q1, Q2, Q3, Q4, Q5, Q6, Q7, Q8, Q9, Q10, Q11, Q12, Q13, Q14, Q15, Q16, Q17, Q18]), "radius" : 3 * mm, "tangentPropagation" : true, "allowEdgeOverflow" : false});
        }
    });
